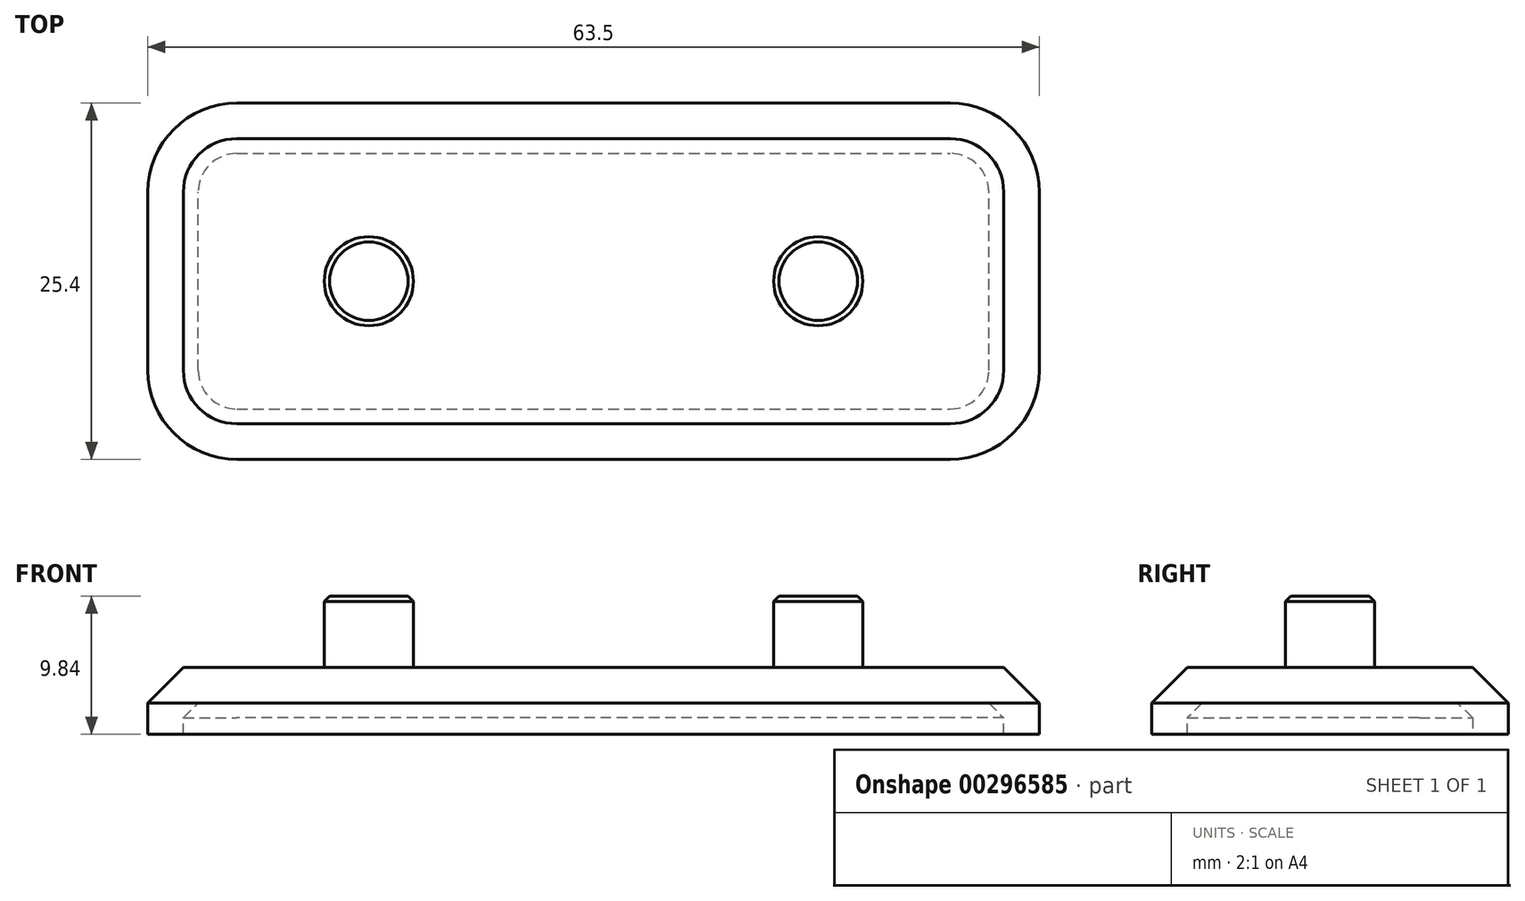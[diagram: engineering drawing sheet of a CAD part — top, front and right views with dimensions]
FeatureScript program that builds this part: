
annotation { "Feature Type Name" : "Feature", "Feature Type Description" : "" }
export const myFeature = defineFeature(function(context is Context, id is Id, definition is map)
    precondition{}
    {
        {
            var Q0;
            Q0=qCreatedBy(makeId("Top.planeOp"),FACE);
            var sketch = newSketch(context, id + "F0", { "sketchPlane" : qUnion([Q0])});
            skLineSegment(sketch, "E0.bottom", {"start": v(6.35, 0) * mm, "end": v(57.15, 0) * mm});
            skLineSegment(sketch, "E0.top", {"start": v(6.35, 25.4) * mm, "end": v(57.15, 25.4) * mm});
            skLineSegment(sketch, "E0.left", {"start": v(0, 6.35) * mm, "end": v(0, 19.05) * mm});
            skLineSegment(sketch, "E0.right", {"start": v(63.5, 6.35) * mm, "end": v(63.5, 19.05) * mm});
            skPoint(sketch, "E1.visualSharp", {"position": v(0, 25.4) * mm});
            skArc(sketch, "E1.filletArc", {"start": v(6.35, 25.4) * mm, "mid": v(1.86, 23.54) * mm, "end": v(0, 19.05) * mm});
            skPoint(sketch, "E2.visualSharp", {"position": v(0, 0) * mm});
            skArc(sketch, "E2.filletArc", {"start": v(0, 6.35) * mm, "mid": v(1.86, 1.86) * mm, "end": v(6.35, 0) * mm});
            skPoint(sketch, "E3.visualSharp", {"position": v(63.5, 25.4) * mm});
            skArc(sketch, "E3.filletArc", {"start": v(63.5, 19.05) * mm, "mid": v(61.64, 23.54) * mm, "end": v(57.15, 25.4) * mm});
            skPoint(sketch, "E4.visualSharp", {"position": v(63.5, 0) * mm});
            skArc(sketch, "E4.filletArc", {"start": v(57.15, 0) * mm, "mid": v(61.64, 1.86) * mm, "end": v(63.5, 6.35) * mm});
            skSolve(sketch);
        }
        {
            var Q0;
            Q0 = qSketchRegion(id + "F0", true);
            extrude(context, id + "F1", {"entities" : qUnion([Q0]), "depth" : 4.76 * mm});
        }
        {
            var Q0;
            Q0=makeQuery(id+"F1.opExtrude","CAP_EDGE",EDGE,{"disambiguationData":[OSD([sQuery(id+"F0.wireOp",EDGE,"E0.bottom")])],"isStart":false});
            chamfer(context, id + "F2", {"entities" : qUnion([Q0]), "width" : 2.54 * mm, "tangentPropagation" : true});
        }
        {
            var Q0;
            Q0=makeQuery(id+"F1.opExtrude","CAP_FACE",FACE,{"disambiguationData":[OSD([sQuery(id+"F0.wireOp",EDGE,"E0.bottom"),sQuery(id+"F0.wireOp",EDGE,"E0.top"),sQuery(id+"F0.wireOp",EDGE,"E0.left"),sQuery(id+"F0.wireOp",EDGE,"E0.right"),sQuery(id+"F0.wireOp",EDGE,"E1.filletArc"),sQuery(id+"F0.wireOp",EDGE,"E2.filletArc"),sQuery(id+"F0.wireOp",EDGE,"E3.filletArc"),sQuery(id+"F0.wireOp",EDGE,"E4.filletArc")])],"isStart":true});
            shell(context, id + "F3", {"entities" : qUnion([Q0]), "thickness" : 2.54 * mm});
        }
        {
            var Q0;
            Q0=makeQuery(id+"F1.opExtrude","CAP_FACE",FACE,{"disambiguationData":[OSD([sQuery(id+"F0.wireOp",EDGE,"E0.bottom"),sQuery(id+"F0.wireOp",EDGE,"E0.top"),sQuery(id+"F0.wireOp",EDGE,"E0.left"),sQuery(id+"F0.wireOp",EDGE,"E0.right"),sQuery(id+"F0.wireOp",EDGE,"E1.filletArc"),sQuery(id+"F0.wireOp",EDGE,"E2.filletArc"),sQuery(id+"F0.wireOp",EDGE,"E3.filletArc"),sQuery(id+"F0.wireOp",EDGE,"E4.filletArc")])],"isStart":false});
            var sketch = newSketch(context, id + "F4", { "sketchPlane" : qUnion([Q0])});
            skCircle(sketch, "E5", {"center": v(15.75, 12.7) * mm, "radius": 10.58 * mm, "construction": true});
            skPoint(sketch, "E5.centerSnap0", {"position": v(6.35, 12.7) * mm});
            skCircle(sketch, "E6", {"center": v(47.75, 12.7) * mm, "radius": 21.17 * mm, "construction": true});
            skLineSegment(sketch, "E7", {"start": v(6.35, 12.7) * mm, "end": v(15.75, 12.7) * mm, "construction": true});
            skLineSegment(sketch, "E8", {"start": v(47.75, 12.7) * mm, "end": v(57.15, 12.7) * mm, "construction": true});
            skCircle(sketch, "E9", {"center": v(15.75, 12.7) * mm, "radius": 3.18 * mm});
            skCircle(sketch, "E10", {"center": v(47.75, 12.7) * mm, "radius": 3.18 * mm});
            skLineSegment(sketch, "E11", {"start": v(26.59, 12.7) * mm, "end": v(26.33, 12.7) * mm, "construction": true});
            skSolve(sketch);
        }
        {
            var Q0;
            Q0 = qSketchRegion(id + "F4", true);
            extrude(context, id + "F5", {"entities" : qUnion([Q0]), "operationType" : NewBodyOperationType.ADD, "flatOperationType" : FlatOperationType.REMOVE, "offsetDistance" : 25.4 * mm, "depth" : 5.08 * mm, "domain" : OperationDomain.MODEL});
        }
        {
            var Q0;
            Q0=makeQuery(id+"F5.opExtrude","CAP_FACE",FACE,{"disambiguationData":[OSD([sQuery(id+"F4.wireOp",EDGE,"E10")])],"isStart":false});
            var Q1;
            Q1=makeQuery(id+"F5.opExtrude","CAP_EDGE",EDGE,{"disambiguationData":[OSD([sQuery(id+"F4.wireOp",EDGE,"E9")])],"isStart":true});
            var Q2;
            Q2=makeQuery(id+"F5.opExtrude","CAP_EDGE",EDGE,{"disambiguationData":[OSD([sQuery(id+"F4.wireOp",EDGE,"E10")])],"isStart":true});
            var Q3;
            Q3=makeQuery(id+"F5.opExtrude","CAP_FACE",FACE,{"disambiguationData":[OSD([sQuery(id+"F4.wireOp",EDGE,"E9")])],"isStart":false});
            chamfer(context, id + "F6", {"entities" : qUnion([Q0, Q1, Q2, Q3]), "width" : 0.38 * mm, "tangentPropagation" : true});
        }
    });
